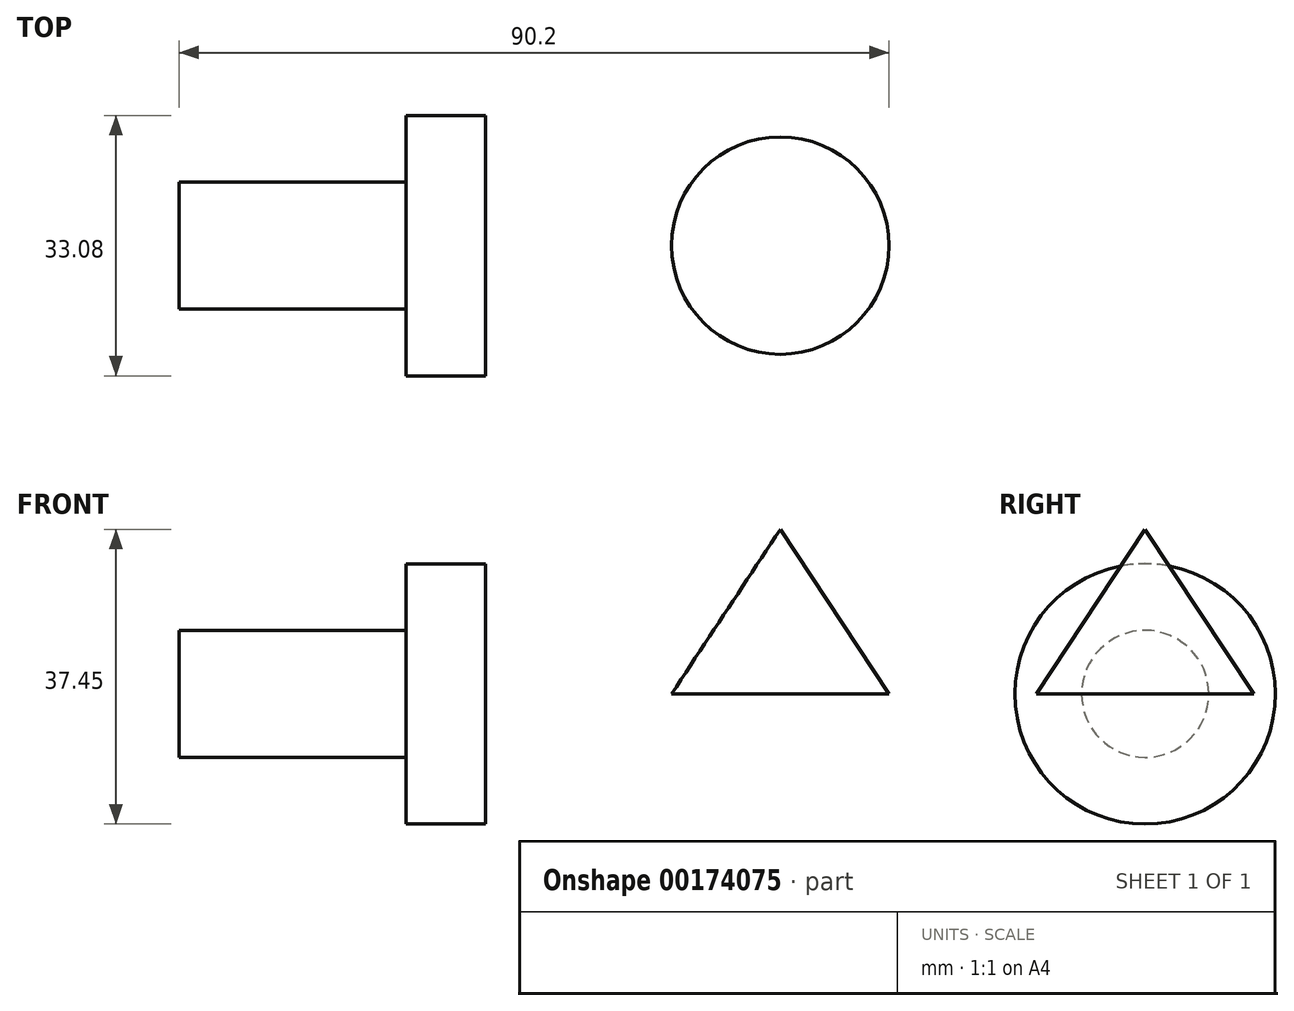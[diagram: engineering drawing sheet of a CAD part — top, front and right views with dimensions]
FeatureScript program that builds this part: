
annotation { "Feature Type Name" : "Feature", "Feature Type Description" : "" }
export const myFeature = defineFeature(function(context is Context, id is Id, definition is map)
    precondition{}
    {
        {
            var Q0;
            Q0=qCreatedBy(makeId("Front.planeOp"),FACE);
            var sketch = newSketch(context, id + "F0", { "sketchPlane" : qUnion([Q0])});
            skLineSegment(sketch, "E0", {"start": v(0, 0) * mm, "end": v(-28.83, 0) * mm});
            skLineSegment(sketch, "E1", {"start": v(-28.83, 0) * mm, "end": v(-28.83, 8.07) * mm});
            skLineSegment(sketch, "E2", {"start": v(-28.83, 8.07) * mm, "end": v(0, 8.07) * mm});
            skLineSegment(sketch, "E3", {"start": v(0, 8.07) * mm, "end": v(0, 16.54) * mm});
            skLineSegment(sketch, "E4", {"start": v(0, 16.54) * mm, "end": v(10.13, 16.54) * mm});
            skLineSegment(sketch, "E5", {"start": v(10.13, 16.54) * mm, "end": v(10.13, 0) * mm});
            skLineSegment(sketch, "E6", {"start": v(10.13, 0) * mm, "end": v(0, 0) * mm});
            skSolve(sketch);
        }
        {
            var Q0;
            Q0=makeQuery(id+"F0.imprint","IMPRINT",FACE,{"disambiguationData":[TD([[makeQuery(id+"F0.imprint","IMPRINT",EDGE,{"derivedFrom":sQuery(id+"F0.wireOp",EDGE,"E0")}),-1.0]])]});
            var Q1;
            Q1=sQuery(id+"F0.wireOp",EDGE,"E6");
            revolve(context, id + "F1", {"entities" : qUnion([Q0]), "axis" : qUnion([Q1]), "revolveType" : RevolveType.FULL});
        }
        {
            var Q0;
            Q0=qCreatedBy(makeId("Front.planeOp"),FACE);
            var sketch = newSketch(context, id + "F2", { "sketchPlane" : qUnion([Q0])});
            skLineSegment(sketch, "E7", {"start": v(47.57, 20.9) * mm, "end": v(47.57, 0) * mm});
            skLineSegment(sketch, "E8", {"start": v(47.57, 0) * mm, "end": v(61.37, 0) * mm});
            skLineSegment(sketch, "E9", {"start": v(61.37, 0) * mm, "end": v(47.57, 20.9) * mm});
            skSolve(sketch);
        }
        {
            var Q0;
            Q0=makeQuery(id+"F2.imprint","IMPRINT",FACE,{"disambiguationData":[TD([[makeQuery(id+"F2.imprint","IMPRINT",EDGE,{"derivedFrom":sQuery(id+"F2.wireOp",EDGE,"E7")}),1.0]])]});
            var Q1;
            Q1=sQuery(id+"F2.wireOp",EDGE,"E7");
            revolve(context, id + "F3", {"entities" : qUnion([Q0]), "axis" : qUnion([Q1]), "revolveType" : RevolveType.FULL});
        }
    });
